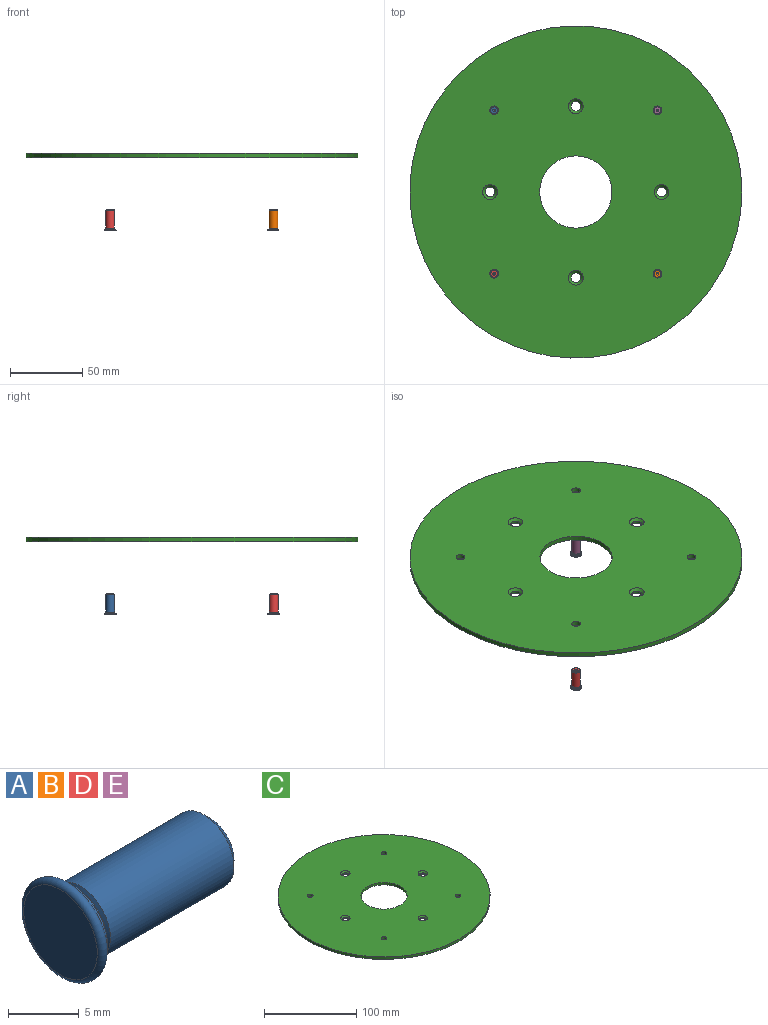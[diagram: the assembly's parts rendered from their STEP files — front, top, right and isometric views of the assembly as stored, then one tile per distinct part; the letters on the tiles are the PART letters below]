
ASSEMBLY  parts=5 mates=4
PART A: 13 faces, bbox 15x8.9x8.9 mm
  f0: cone r=0.45mm half-angle=60deg, axis (1,0,0), area 2.9mm2, adj f1
  f1: plane 4.77x4.77mm, normal (1,0,0), area 15.3mm2, adj f0,f2
  f2: cone r=2.69mm half-angle=45deg, axis (-1,0,0), area 14.7mm2, adj f1,f3
  f3: cylinder r=3mm len=12.39mm, axis (-1,0,0), area 233.5mm2, adj f2,f4
  f4: cone r=2.85mm half-angle=63.4deg, axis (1,0,0), area 6mm2, adj f3,f5
  f5: torus R=2.83mm, axis (-1,0,0), area 2.7mm2, adj f4,f6
  f6: cone r=2.85mm half-angle=63.4deg, axis (-1,0,0), area 6mm2, adj f5,f7
  f7: cylinder r=3mm len=6mm, axis (-1,0,0), area 6mm2, adj f6,f8
  f8: plane 6.97x6.97mm, normal (1,0,0), area 9.9mm2, adj f7,f9
  f9: cylinder r=3.48mm len=6.97mm, axis (1,0,0), area 9mm2, adj f8,f12
  f10: plane 7.38x7.38mm, normal (-1,0,0), area 42.8mm2, adj f11
  f11: torus R=3.69mm, axis (-1,0,0), area 32mm2, adj f10,f12
  f12: plane 7.38x7.38mm, normal (1,0,0), area 4.6mm2, adj f9,f11
PART B: same geometry as A
PART C: 16 faces, bbox 230x230x3.2 mm
  f0: cylinder r=3mm len=6mm, axis (0,0,1), area 59.8mm2, adj f11,f12
  f1: cylinder r=3mm len=6mm, axis (0,0,1), area 59.8mm2, adj f11,f12
  f2: cylinder r=3mm len=6mm, axis (0,0,1), area 59.8mm2, adj f11,f12
  f3: cylinder r=3.4mm len=6.8mm, axis (0,0,1), area 31.4mm2, adj f4,f12
  f4: cone r=3.4mm half-angle=45deg, axis (0,0,1), area 64.5mm2, adj f3,f11
  f5: cylinder r=3.4mm len=6.8mm, axis (0,0,1), area 31.4mm2, adj f6,f12
  f6: cone r=3.4mm half-angle=45deg, axis (0,0,1), area 64.5mm2, adj f5,f11
  f7: cylinder r=3.4mm len=6.8mm, axis (0,0,1), area 31.4mm2, adj f8,f12
  f8: cone r=3.4mm half-angle=45deg, axis (0,0,1), area 64.5mm2, adj f7,f11
  f9: cylinder r=25mm len=50mm, axis (0,0,-1), area 498.7mm2, adj f11,f12
  f10: cylinder r=115mm len=230mm, axis (0,0,-1), area 2294.1mm2, adj f11,f12
  f11: plane 230x230mm, normal (0,0,1), area 39143.2mm2, adj f0,f1,f2,f4,f6,f8,f9,f10
  f12: plane 230x230mm, normal (0,0,-1), area 39325.7mm2, adj f0,f1,f2,f3,f5,f7,f9,f10
  f13: cylinder r=3.4mm len=6.8mm, axis (0,0,1), area 31.4mm2, adj f12,f14
  f14: cone r=3.4mm half-angle=45deg, axis (0,0,1), area 64.5mm2, adj f11,f13
  f15: cylinder r=3mm len=6mm, axis (0,0,1), area 59.8mm2, adj f11,f12
PART D: same geometry as A
PART E: same geometry as A
PLACE A rot(axis=(0,-1,0),90deg) t=(-120.03,32.7,-38.14)mm
PLACE B rot(axis=(0,-1,0),90deg) t=(-6.9,-80.44,-38.14)mm
PLACE C t=(-63.47,-23.87,12.66)mm
PLACE D rot(axis=(0,-1,0),90deg) t=(-120.03,-80.44,-38.14)mm
PLACE E rot(axis=(0,-1,0),90deg) t=(-6.9,32.7,-38.14)mm
MATE cylindrical B.f3 <-> C.f0  axis (0,0,-1) through (-6.9,-80.44,-38.14)mm
MATE cylindrical D.f3 <-> C.f1  axis (0,0,-1) through (-120.03,-80.44,-38.14)mm
MATE cylindrical A.f3 <-> C.f2  axis (0,0,-1) through (-120.03,32.7,-38.14)mm
MATE cylindrical E.f3 <-> C.f15  axis (0,0,-1) through (-6.9,32.7,-38.14)mm
